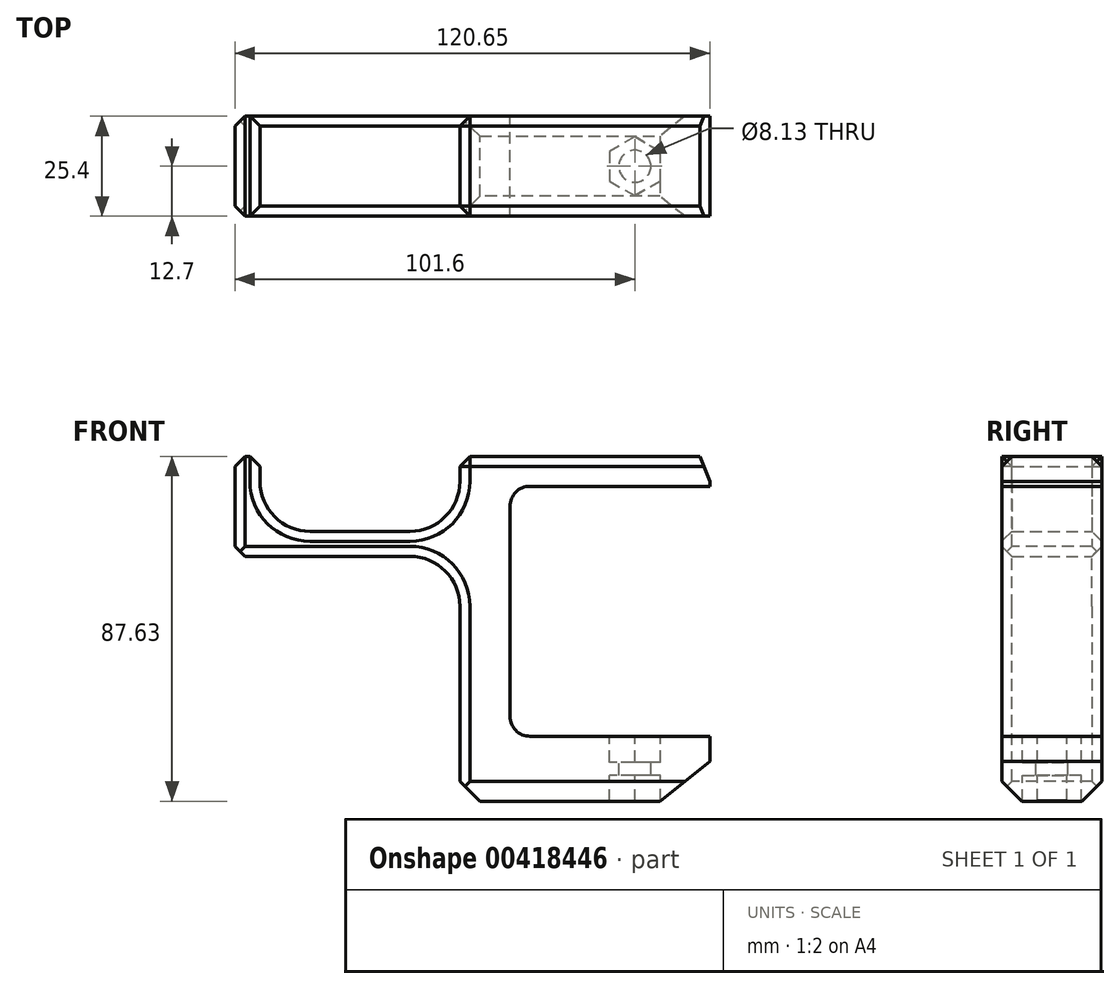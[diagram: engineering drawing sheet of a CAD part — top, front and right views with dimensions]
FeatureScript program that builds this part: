
annotation { "Feature Type Name" : "Feature", "Feature Type Description" : "" }
export const myFeature = defineFeature(function(context is Context, id is Id, definition is map)
    precondition{}
    {
        {
            var Q0;
            Q0=qCreatedBy(makeId("Front.planeOp"),FACE);
            var sketch = newSketch(context, id + "F0", { "sketchPlane" : qUnion([Q0])});
            skLineSegment(sketch, "E0.bottom", {"start": v(0, 44.53) * mm, "end": v(-12.7, 44.53) * mm});
            skLineSegment(sketch, "E0.top", {"start": v(0, -43.1) * mm, "end": v(-12.7, -43.1) * mm});
            skLineSegment(sketch, "E0.left", {"start": v(0, 44.53) * mm, "end": v(0, -43.1) * mm});
            skLineSegment(sketch, "E0.right", {"start": v(-12.7, 44.53) * mm, "end": v(-12.7, -43.1) * mm});
            skLineSegment(sketch, "E1.bottom", {"start": v(0, 44.53) * mm, "end": v(50.8, 44.53) * mm});
            skLineSegment(sketch, "E1.top", {"start": v(0, 36.9) * mm, "end": v(50.8, 36.9) * mm});
            skLineSegment(sketch, "E1.left", {"start": v(0, 44.53) * mm, "end": v(0, 36.9) * mm});
            skLineSegment(sketch, "E1.right", {"start": v(50.8, 44.53) * mm, "end": v(50.8, 36.9) * mm});
            skLineSegment(sketch, "E2.bottom", {"start": v(0, -43.1) * mm, "end": v(50.8, -43.1) * mm});
            skLineSegment(sketch, "E2.top", {"start": v(0, -26.6) * mm, "end": v(50.8, -26.6) * mm});
            skLineSegment(sketch, "E2.left", {"start": v(0, -43.1) * mm, "end": v(0, -26.6) * mm});
            skLineSegment(sketch, "E2.right", {"start": v(50.8, -43.1) * mm, "end": v(50.8, -26.6) * mm});
            skLineSegment(sketch, "E3.bottom", {"start": v(-12.7, 25.48) * mm, "end": v(-63.5, 25.48) * mm});
            skLineSegment(sketch, "E3.top", {"start": v(-12.7, 19.13) * mm, "end": v(-63.5, 19.13) * mm});
            skLineSegment(sketch, "E3.left", {"start": v(-12.7, 25.48) * mm, "end": v(-12.7, 19.13) * mm});
            skLineSegment(sketch, "E3.right", {"start": v(-63.5, 25.48) * mm, "end": v(-63.5, 19.13) * mm});
            skLineSegment(sketch, "E4.bottom", {"start": v(-63.5, 19.13) * mm, "end": v(-69.85, 19.13) * mm});
            skLineSegment(sketch, "E4.top", {"start": v(-63.5, 44.53) * mm, "end": v(-69.85, 44.53) * mm});
            skLineSegment(sketch, "E4.left", {"start": v(-63.5, 19.13) * mm, "end": v(-63.5, 44.53) * mm});
            skLineSegment(sketch, "E4.right", {"start": v(-69.85, 19.13) * mm, "end": v(-69.85, 44.53) * mm});
            skSolve(sketch);
        }
        {
            var Q0;
            {var subQ3=sQuery(id+"F0.wireOp",EDGE,"E4.bottom");Q0=makeQuery(id+"F0.imprint","IMPRINT",FACE,{"disambiguationData":[TD([[makeQuery(id+"F0.imprint","IMPRINT",EDGE,{"derivedFrom":subQ3}),-1.0]])]});}
            var Q1;
            {var subQ0=sQuery(id+"F0.wireOp",EDGE,"E3.bottom");Q1=makeQuery(id+"F0.imprint","IMPRINT",FACE,{"disambiguationData":[TD([[makeQuery(id+"F0.imprint","IMPRINT",EDGE,{"derivedFrom":subQ0}),1.0]])]});}
            var Q2;
            {var subQ1=sQuery(id+"F0.wireOp",EDGE,"E0.bottom");Q2=makeQuery(id+"F0.imprint","IMPRINT",FACE,{"disambiguationData":[TD([[makeQuery(id+"F0.imprint","IMPRINT",EDGE,{"derivedFrom":subQ1}),1.0]])]});}
            var Q3;
            Q3=makeQuery(id+"F0.imprint","IMPRINT",FACE,{"disambiguationData":[TD([[makeQuery(id+"F0.imprint","IMPRINT",EDGE,{"derivedFrom":sQuery(id+"F0.wireOp",EDGE,"E1.bottom")}),-1.0]])]});
            var Q4;
            Q4=makeQuery(id+"F0.imprint","IMPRINT",FACE,{"disambiguationData":[TD([[makeQuery(id+"F0.imprint","IMPRINT",EDGE,{"derivedFrom":sQuery(id+"F0.wireOp",EDGE,"E2.bottom")}),1.0]])]});
            extrude(context, id + "F1", {"entities" : qUnion([Q0, Q1, Q2, Q3, Q4]), "depth" : 25.4 * mm});
        }
        {
            var Q0;
            Q0=makeQuery(id+"F1.opExtrude","SWEPT_EDGE",EDGE,{"disambiguationData":[OSD([sQuery(id+"F0.wireOp",EDGE,"E0.right"),sQuery(id+"F0.wireOp",EDGE,"E3.bottom"),sQuery(id+"F0.wireOp",EDGE,"E3.left")])]});
            var Q1;
            Q1=makeQuery(id+"F1.opExtrude","SWEPT_EDGE",EDGE,{"disambiguationData":[OSD([sQuery(id+"F0.wireOp",EDGE,"E3.bottom"),sQuery(id+"F0.wireOp",EDGE,"E4.left")])]});
            fillet(context, id + "F2", {"entities" : qUnion([Q0, Q1]), "radius" : 12.7 * mm, "tangentPropagation" : true, "allowEdgeOverflow" : false});
        }
        {
            var Q0;
            Q0=makeQuery(id+"F1.opExtrude","SWEPT_EDGE",EDGE,{"disambiguationData":[OSD([sQuery(id+"F0.wireOp",EDGE,"E4.top"),sQuery(id+"F0.wireOp",EDGE,"E4.left")])]});
            var Q1;
            Q1=makeQuery(id+"F1.opExtrude","CAP_EDGE",EDGE,{"disambiguationData":[OSD([sQuery(id+"F0.wireOp",EDGE,"E4.right")])],"isStart":true});
            var Q2;
            Q2=makeQuery(id+"F1.opExtrude","SWEPT_EDGE",EDGE,{"disambiguationData":[OSD([sQuery(id+"F0.wireOp",EDGE,"E4.top"),sQuery(id+"F0.wireOp",EDGE,"E4.right")])]});
            var Q3;
            Q3=makeQuery(id+"F1.opExtrude","CAP_EDGE",EDGE,{"disambiguationData":[OSD([sQuery(id+"F0.wireOp",EDGE,"E4.right")])],"isStart":false});
            var Q4;
            {var subQ0=sQuery(id+"F0.wireOp",EDGE,"E4.left");var subQ1=sQuery(id+"F0.wireOp",EDGE,"E3.bottom");Q4=makeQuery(id+"F2.opFillet","BLEND_EDGE",EDGE,{"blendedFrom":[makeQuery(id+"F1.opExtrude","SWEPT_EDGE",EDGE,{"disambiguationData":[OSD([subQ1,subQ0])]}),makeQuery(id+"F1.opExtrude","CAP_FACE",FACE,{"disambiguationData":[OSD([sQuery(id+"F0.wireOp",EDGE,"E0.bottom"),sQuery(id+"F0.wireOp",EDGE,"E0.top"),sQuery(id+"F0.wireOp",EDGE,"E0.left"),sQuery(id+"F0.wireOp",EDGE,"E0.right"),sQuery(id+"F0.wireOp",EDGE,"E1.bottom"),sQuery(id+"F0.wireOp",EDGE,"E1.top"),sQuery(id+"F0.wireOp",EDGE,"E1.right"),sQuery(id+"F0.wireOp",EDGE,"E2.bottom"),sQuery(id+"F0.wireOp",EDGE,"E2.top"),sQuery(id+"F0.wireOp",EDGE,"E2.right"),subQ1,sQuery(id+"F0.wireOp",EDGE,"E3.top"),sQuery(id+"F0.wireOp",EDGE,"E4.bottom"),sQuery(id+"F0.wireOp",EDGE,"E4.top"),subQ0,sQuery(id+"F0.wireOp",EDGE,"E4.right")])],"isStart":false})],"blendedInto":[makeQuery(id+"F1.opExtrude","CAP_FACE",FACE,{"disambiguationData":[OSD([sQuery(id+"F0.wireOp",EDGE,"E0.bottom"),sQuery(id+"F0.wireOp",EDGE,"E0.top"),sQuery(id+"F0.wireOp",EDGE,"E0.left"),sQuery(id+"F0.wireOp",EDGE,"E0.right"),sQuery(id+"F0.wireOp",EDGE,"E1.bottom"),sQuery(id+"F0.wireOp",EDGE,"E1.top"),sQuery(id+"F0.wireOp",EDGE,"E1.right"),sQuery(id+"F0.wireOp",EDGE,"E2.bottom"),sQuery(id+"F0.wireOp",EDGE,"E2.top"),sQuery(id+"F0.wireOp",EDGE,"E2.right"),subQ1,sQuery(id+"F0.wireOp",EDGE,"E3.top"),sQuery(id+"F0.wireOp",EDGE,"E4.bottom"),sQuery(id+"F0.wireOp",EDGE,"E4.top"),subQ0,sQuery(id+"F0.wireOp",EDGE,"E4.right")])],"isStart":false})]});}
            var Q5;
            Q5=makeQuery(id+"F1.opExtrude","CAP_EDGE",EDGE,{"disambiguationData":[OSD([sQuery(id+"F0.wireOp",EDGE,"E3.bottom")])],"isStart":true});
            var Q6;
            Q6=makeQuery(id+"F1.opExtrude","SWEPT_EDGE",EDGE,{"disambiguationData":[OSD([sQuery(id+"F0.wireOp",EDGE,"E0.bottom"),sQuery(id+"F0.wireOp",EDGE,"E0.right")])]});
            var Q7;
            Q7=makeQuery(id+"F1.opExtrude","CAP_EDGE",EDGE,{"disambiguationData":[OSD([sQuery(id+"F0.wireOp",EDGE,"E0.bottom"),sQuery(id+"F0.wireOp",EDGE,"E1.bottom")])],"isStart":false});
            var Q8;
            Q8=makeQuery(id+"F1.opExtrude","CAP_EDGE",EDGE,{"disambiguationData":[OSD([sQuery(id+"F0.wireOp",EDGE,"E0.bottom"),sQuery(id+"F0.wireOp",EDGE,"E1.bottom")])],"isStart":true});
            var Q9;
            Q9=makeQuery(id+"F1.opExtrude","SWEPT_FACE",FACE,{"disambiguationData":[OSD([sQuery(id+"F0.wireOp",EDGE,"E4.right")])]});
            chamfer(context, id + "F3", {"entities" : qUnion([Q0, Q1, Q2, Q3, Q4, Q5, Q6, Q7, Q8, Q9]), "width" : 2.54 * mm, "tangentPropagation" : true});
        }
        {
            var Q0;
            Q0=makeQuery(id+"F1.opExtrude","SWEPT_EDGE",EDGE,{"disambiguationData":[OSD([sQuery(id+"F0.wireOp",EDGE,"E0.right"),sQuery(id+"F0.wireOp",EDGE,"E3.top"),sQuery(id+"F0.wireOp",EDGE,"E3.left")])]});
            fillet(context, id + "F4", {"entities" : qUnion([Q0]), "radius" : 12.7 * mm, "tangentPropagation" : true, "allowEdgeOverflow" : false});
        }
        {
            var Q0;
            {var subQ0=sQuery(id+"F0.wireOp",EDGE,"E0.right");Q0=makeQuery(id+"F1.opExtrude","CAP_EDGE",EDGE,{"disambiguationData":[OSD([subQ0]),TDD([makeQuery(id+"F0.imprint","IMPRINT",EDGE,{"disambiguationData":[TD([[makeQuery(id+"F0.imprint","INTERSECT",VERTEX,{"derivedFrom":[sQuery(id+"F0.wireOp",EDGE,"E0.top"),subQ0]}),1.0]])],"derivedFrom":subQ0})])],"isStart":false});}
            var Q1;
            {var subQ0=sQuery(id+"F0.wireOp",EDGE,"E0.right");Q1=makeQuery(id+"F1.opExtrude","CAP_EDGE",EDGE,{"disambiguationData":[OSD([subQ0]),TDD([makeQuery(id+"F0.imprint","IMPRINT",EDGE,{"disambiguationData":[TD([[makeQuery(id+"F0.imprint","INTERSECT",VERTEX,{"derivedFrom":[sQuery(id+"F0.wireOp",EDGE,"E0.top"),subQ0]}),1.0]])],"derivedFrom":subQ0})])],"isStart":true});}
            chamfer(context, id + "F5", {"entities" : qUnion([Q0, Q1]), "width" : 2.54 * mm, "tangentPropagation" : true});
        }
        {
            var Q0;
            Q0=makeQuery(id+"F1.opExtrude","SWEPT_EDGE",EDGE,{"disambiguationData":[OSD([sQuery(id+"F0.wireOp",EDGE,"E0.left"),sQuery(id+"F0.wireOp",EDGE,"E1.top"),sQuery(id+"F0.wireOp",EDGE,"E1.left")])]});
            var Q1;
            Q1=makeQuery(id+"F1.opExtrude","SWEPT_EDGE",EDGE,{"disambiguationData":[OSD([sQuery(id+"F0.wireOp",EDGE,"E0.left"),sQuery(id+"F0.wireOp",EDGE,"E2.top"),sQuery(id+"F0.wireOp",EDGE,"E2.left")])]});
            fillet(context, id + "F6", {"entities" : qUnion([Q0, Q1]), "radius" : 5.08 * mm, "tangentPropagation" : true, "allowEdgeOverflow" : false});
        }
        {
            var Q0;
            Q0=makeQuery(id+"F1.opExtrude","SWEPT_FACE",FACE,{"disambiguationData":[OSD([sQuery(id+"F0.wireOp",EDGE,"E2.top")])]});
            var sketch = newSketch(context, id + "F7", { "sketchPlane" : qUnion([Q0])});
            skPoint(sketch, "E5", {"position": v(31.75, -12.7) * mm});
            skCircle(sketch, "E6", {"center": v(31.75, -12.7) * mm, "radius": 6.48 * mm});
            skCircle(sketch, "E7.cCircle", {"center": v(31.75, -12.7) * mm, "radius": 6.48 * mm, "construction": true});
            skLineSegment(sketch, "E7.0", {"start": v(31.75, -5.22) * mm, "end": v(38.23, -8.96) * mm});
            skLineSegment(sketch, "E7.1", {"start": v(38.23, -8.96) * mm, "end": v(38.23, -16.44) * mm});
            skLineSegment(sketch, "E7.2", {"start": v(38.23, -16.44) * mm, "end": v(31.75, -20.18) * mm});
            skLineSegment(sketch, "E7.3", {"start": v(31.75, -20.18) * mm, "end": v(25.27, -16.44) * mm});
            skLineSegment(sketch, "E7.4", {"start": v(25.27, -16.44) * mm, "end": v(25.27, -8.96) * mm});
            skLineSegment(sketch, "E7.5", {"start": v(25.27, -8.96) * mm, "end": v(31.75, -5.22) * mm});
            skPoint(sketch, "E7.0.midPoint", {"position": v(34.99, -7.1) * mm});
            skSolve(sketch);
        }
        {
            var Q0;
            {var subQ0=sQuery(id+"F0.wireOp",EDGE,"E0.top");var subQ1=sQuery(id+"F0.wireOp",EDGE,"E0.right");Q0=makeQuery(id+"F5.opChamfer","BLEND_EDGE",EDGE,{"blendedFrom":[makeQuery(id+"F1.opExtrude","CAP_EDGE",EDGE,{"disambiguationData":[OSD([subQ1]),TDD([makeQuery(id+"F0.imprint","IMPRINT",EDGE,{"disambiguationData":[TD([[makeQuery(id+"F0.imprint","INTERSECT",VERTEX,{"derivedFrom":[subQ0,subQ1]}),1.0]])],"derivedFrom":subQ1})])],"isStart":false}),makeQuery(id+"F1.opExtrude","SWEPT_FACE",FACE,{"disambiguationData":[OSD([subQ0,sQuery(id+"F0.wireOp",EDGE,"E2.bottom")])]})],"blendedInto":[makeQuery(id+"F1.opExtrude","SWEPT_FACE",FACE,{"disambiguationData":[OSD([subQ0,sQuery(id+"F0.wireOp",EDGE,"E2.bottom")])]})]});}
            var Q1;
            Q1=makeQuery(id+"F1.opExtrude","SWEPT_EDGE",EDGE,{"disambiguationData":[OSD([sQuery(id+"F0.wireOp",EDGE,"E0.top"),sQuery(id+"F0.wireOp",EDGE,"E0.right")])]});
            var Q2;
            {var subQ0=sQuery(id+"F0.wireOp",EDGE,"E0.top");var subQ1=sQuery(id+"F0.wireOp",EDGE,"E0.right");Q2=makeQuery(id+"F5.opChamfer","BLEND_EDGE",EDGE,{"blendedFrom":[makeQuery(id+"F1.opExtrude","CAP_EDGE",EDGE,{"disambiguationData":[OSD([subQ1]),TDD([makeQuery(id+"F0.imprint","IMPRINT",EDGE,{"disambiguationData":[TD([[makeQuery(id+"F0.imprint","INTERSECT",VERTEX,{"derivedFrom":[subQ0,subQ1]}),1.0]])],"derivedFrom":subQ1})])],"isStart":true}),makeQuery(id+"F1.opExtrude","SWEPT_FACE",FACE,{"disambiguationData":[OSD([subQ0,sQuery(id+"F0.wireOp",EDGE,"E2.bottom")])]})],"blendedInto":[makeQuery(id+"F1.opExtrude","SWEPT_FACE",FACE,{"disambiguationData":[OSD([subQ0,sQuery(id+"F0.wireOp",EDGE,"E2.bottom")])]})]});}
            var Q3;
            Q3=makeQuery(id+"F1.opExtrude","CAP_EDGE",EDGE,{"disambiguationData":[OSD([sQuery(id+"F0.wireOp",EDGE,"E0.top"),sQuery(id+"F0.wireOp",EDGE,"E2.bottom")])],"isStart":true});
            var Q4;
            Q4=makeQuery(id+"F1.opExtrude","CAP_EDGE",EDGE,{"disambiguationData":[OSD([sQuery(id+"F0.wireOp",EDGE,"E0.top"),sQuery(id+"F0.wireOp",EDGE,"E2.bottom")])],"isStart":false});
            chamfer(context, id + "F8", {"entities" : qUnion([Q0, Q1, Q2, Q3, Q4]), "width" : 5.08 * mm, "tangentPropagation" : true});
        }
        {
            var Q0;
            Q0=makeQuery(id+"F1.opExtrude","SWEPT_EDGE",EDGE,{"disambiguationData":[OSD([sQuery(id+"F0.wireOp",EDGE,"E2.bottom"),sQuery(id+"F0.wireOp",EDGE,"E2.right")])]});
            chamfer(context, id + "F9", {"entities" : qUnion([Q0]), "chamferType" : ChamferType.TWO_OFFSETS, "width1" : 10.16 * mm, "oppositeDirection" : false, "width2" : 12.7 * mm, "tangentPropagation" : true});
        }
        {
            var Q0;
            Q0=makeQuery(id+"F1.opExtrude","SWEPT_EDGE",EDGE,{"disambiguationData":[OSD([sQuery(id+"F0.wireOp",EDGE,"E1.bottom"),sQuery(id+"F0.wireOp",EDGE,"E1.right")])]});
            chamfer(context, id + "F10", {"entities" : qUnion([Q0]), "chamferType" : ChamferType.TWO_OFFSETS, "width1" : 2.54 * mm, "oppositeDirection" : false, "width2" : 6.35 * mm, "tangentPropagation" : true});
        }
        {
            var Q0;
            {var subQ0=sQuery(id+"F7.wireOp",EDGE,"E7.4");var subQ1=sQuery(id+"F7.wireOp",EDGE,"E6");var subQ2=makeQuery(id+"F7.imprint","INTERSECT",VERTEX,{"derivedFrom":[subQ1,subQ0]});Q0=makeQuery(id+"F7.imprint","IMPRINT",FACE,{"disambiguationData":[TD([[makeQuery(id+"F7.imprint","IMPRINT",EDGE,{"disambiguationData":[TD([[subQ2,-1.0]])],"derivedFrom":subQ1}),-1.0]])]});}
            var Q1;
            {var subQ0=sQuery(id+"F7.wireOp",EDGE,"E7.5");var subQ1=sQuery(id+"F7.wireOp",EDGE,"E6");var subQ2=makeQuery(id+"F7.imprint","INTERSECT",VERTEX,{"derivedFrom":[subQ1,subQ0]});Q1=makeQuery(id+"F7.imprint","IMPRINT",FACE,{"disambiguationData":[TD([[makeQuery(id+"F7.imprint","IMPRINT",EDGE,{"disambiguationData":[TD([[subQ2,-1.0]])],"derivedFrom":subQ1}),-1.0]])]});}
            var Q2;
            {var subQ0=sQuery(id+"F7.wireOp",EDGE,"E7.0");var subQ1=sQuery(id+"F7.wireOp",EDGE,"E6");var subQ2=makeQuery(id+"F7.imprint","INTERSECT",VERTEX,{"derivedFrom":[subQ1,subQ0]});Q2=makeQuery(id+"F7.imprint","IMPRINT",FACE,{"disambiguationData":[TD([[makeQuery(id+"F7.imprint","IMPRINT",EDGE,{"disambiguationData":[TD([[subQ2,-1.0]])],"derivedFrom":subQ1}),-1.0]])]});}
            var Q3;
            {var subQ0=sQuery(id+"F7.wireOp",EDGE,"E7.0");var subQ1=sQuery(id+"F7.wireOp",EDGE,"E6");var subQ2=makeQuery(id+"F7.imprint","INTERSECT",VERTEX,{"derivedFrom":[subQ1,subQ0]});Q3=makeQuery(id+"F7.imprint","IMPRINT",FACE,{"disambiguationData":[TD([[makeQuery(id+"F7.imprint","IMPRINT",EDGE,{"disambiguationData":[TD([[subQ2,1.0]])],"derivedFrom":subQ1}),-1.0]])]});}
            var Q4;
            {var subQ0=sQuery(id+"F7.wireOp",EDGE,"E7.1");var subQ1=sQuery(id+"F7.wireOp",EDGE,"E6");var subQ2=makeQuery(id+"F7.imprint","INTERSECT",VERTEX,{"derivedFrom":[subQ1,subQ0]});Q4=makeQuery(id+"F7.imprint","IMPRINT",FACE,{"disambiguationData":[TD([[makeQuery(id+"F7.imprint","IMPRINT",EDGE,{"disambiguationData":[TD([[subQ2,1.0]])],"derivedFrom":subQ1}),-1.0]])]});}
            var Q5;
            {var subQ0=sQuery(id+"F7.wireOp",EDGE,"E7.3");var subQ1=sQuery(id+"F7.wireOp",EDGE,"E6");var subQ2=makeQuery(id+"F7.imprint","INTERSECT",VERTEX,{"derivedFrom":[subQ1,subQ0]});Q5=makeQuery(id+"F7.imprint","IMPRINT",FACE,{"disambiguationData":[TD([[makeQuery(id+"F7.imprint","IMPRINT",EDGE,{"disambiguationData":[TD([[subQ2,-1.0]])],"derivedFrom":subQ1}),-1.0]])]});}
            var Q6;
            {var subQ0=sQuery(id+"F7.wireOp",EDGE,"E6");var subQ4=makeQuery(id+"F7.imprint","INTERSECT",VERTEX,{"derivedFrom":[subQ0,sQuery(id+"F7.wireOp",EDGE,"E7.0")]});Q6=makeQuery(id+"F7.imprint","IMPRINT",FACE,{"disambiguationData":[TD([[makeQuery(id+"F7.imprint","IMPRINT",EDGE,{"disambiguationData":[TD([[subQ4,1.0]])],"derivedFrom":subQ0}),1.0]])]});}
            extrude(context, id + "F11", {"entities" : qUnion([Q0, Q1, Q2, Q3, Q4, Q5, Q6]), "operationType" : NewBodyOperationType.REMOVE, "oppositeDirection" : true, "depth" : 6.6 * mm});
        }
        {
            var Q0;
            {var subQ0=sQuery(id+"F7.wireOp",EDGE,"E6");var subQ4=makeQuery(id+"F7.imprint","INTERSECT",VERTEX,{"derivedFrom":[subQ0,sQuery(id+"F7.wireOp",EDGE,"E7.0")]});Q0=makeQuery(id+"F7.imprint","IMPRINT",FACE,{"disambiguationData":[TD([[makeQuery(id+"F7.imprint","IMPRINT",EDGE,{"disambiguationData":[TD([[subQ4,1.0]])],"derivedFrom":subQ0}),1.0]])]});}
            var Q1;
            {var subQ0=sQuery(id+"F7.wireOp",EDGE,"E7.1");var subQ1=sQuery(id+"F7.wireOp",EDGE,"E6");var subQ2=makeQuery(id+"F7.imprint","INTERSECT",VERTEX,{"derivedFrom":[subQ1,subQ0]});Q1=makeQuery(id+"F7.imprint","IMPRINT",FACE,{"disambiguationData":[TD([[makeQuery(id+"F7.imprint","IMPRINT",EDGE,{"disambiguationData":[TD([[subQ2,1.0]])],"derivedFrom":subQ1}),-1.0]])]});}
            var Q2;
            {var subQ0=sQuery(id+"F7.wireOp",EDGE,"E7.0");var subQ1=sQuery(id+"F7.wireOp",EDGE,"E6");var subQ2=makeQuery(id+"F7.imprint","INTERSECT",VERTEX,{"derivedFrom":[subQ1,subQ0]});Q2=makeQuery(id+"F7.imprint","IMPRINT",FACE,{"disambiguationData":[TD([[makeQuery(id+"F7.imprint","IMPRINT",EDGE,{"disambiguationData":[TD([[subQ2,-1.0]])],"derivedFrom":subQ1}),-1.0]])]});}
            var Q3;
            {var subQ0=sQuery(id+"F7.wireOp",EDGE,"E7.0");var subQ1=sQuery(id+"F7.wireOp",EDGE,"E6");var subQ2=makeQuery(id+"F7.imprint","INTERSECT",VERTEX,{"derivedFrom":[subQ1,subQ0]});Q3=makeQuery(id+"F7.imprint","IMPRINT",FACE,{"disambiguationData":[TD([[makeQuery(id+"F7.imprint","IMPRINT",EDGE,{"disambiguationData":[TD([[subQ2,1.0]])],"derivedFrom":subQ1}),-1.0]])]});}
            var Q4;
            {var subQ0=sQuery(id+"F7.wireOp",EDGE,"E7.5");var subQ1=sQuery(id+"F7.wireOp",EDGE,"E6");var subQ2=makeQuery(id+"F7.imprint","INTERSECT",VERTEX,{"derivedFrom":[subQ1,subQ0]});Q4=makeQuery(id+"F7.imprint","IMPRINT",FACE,{"disambiguationData":[TD([[makeQuery(id+"F7.imprint","IMPRINT",EDGE,{"disambiguationData":[TD([[subQ2,-1.0]])],"derivedFrom":subQ1}),-1.0]])]});}
            var Q5;
            {var subQ0=sQuery(id+"F7.wireOp",EDGE,"E7.4");var subQ1=sQuery(id+"F7.wireOp",EDGE,"E6");var subQ2=makeQuery(id+"F7.imprint","INTERSECT",VERTEX,{"derivedFrom":[subQ1,subQ0]});Q5=makeQuery(id+"F7.imprint","IMPRINT",FACE,{"disambiguationData":[TD([[makeQuery(id+"F7.imprint","IMPRINT",EDGE,{"disambiguationData":[TD([[subQ2,-1.0]])],"derivedFrom":subQ1}),-1.0]])]});}
            var Q6;
            {var subQ0=sQuery(id+"F7.wireOp",EDGE,"E7.3");var subQ1=sQuery(id+"F7.wireOp",EDGE,"E6");var subQ2=makeQuery(id+"F7.imprint","INTERSECT",VERTEX,{"derivedFrom":[subQ1,subQ0]});Q6=makeQuery(id+"F7.imprint","IMPRINT",FACE,{"disambiguationData":[TD([[makeQuery(id+"F7.imprint","IMPRINT",EDGE,{"disambiguationData":[TD([[subQ2,-1.0]])],"derivedFrom":subQ1}),-1.0]])]});}
            extrude(context, id + "F12", {"entities" : qUnion([Q0, Q1, Q2, Q3, Q4, Q5, Q6]), "operationType" : NewBodyOperationType.REMOVE, "endBound" : BoundingType.THROUGH_ALL, "oppositeDirection" : true, "depth" : -9.9 * mm, "hasSecondDirection" : true, "secondDirectionOppositeDirection" : true, "secondDirectionDepth" : 9.9 * mm});
        }
        {
            var Q0;
            Q0=sQuery(id+"F7.wireOp",VERTEX,"E5");
            var Q1;
            Q1=makeQuery(id+"F1.opExtrude","SWEPT_BODY",BODY,{"disambiguationData":[OSD([sQuery(id+"F0.wireOp",EDGE,"E0.bottom"),sQuery(id+"F0.wireOp",EDGE,"E0.top"),sQuery(id+"F0.wireOp",EDGE,"E0.left"),sQuery(id+"F0.wireOp",EDGE,"E0.right"),sQuery(id+"F0.wireOp",EDGE,"E1.bottom"),sQuery(id+"F0.wireOp",EDGE,"E1.top"),sQuery(id+"F0.wireOp",EDGE,"E1.right"),sQuery(id+"F0.wireOp",EDGE,"E2.bottom"),sQuery(id+"F0.wireOp",EDGE,"E2.top"),sQuery(id+"F0.wireOp",EDGE,"E2.right"),sQuery(id+"F0.wireOp",EDGE,"E3.bottom"),sQuery(id+"F0.wireOp",EDGE,"E3.top"),sQuery(id+"F0.wireOp",EDGE,"E4.bottom"),sQuery(id+"F0.wireOp",EDGE,"E4.top"),sQuery(id+"F0.wireOp",EDGE,"E4.left"),sQuery(id+"F0.wireOp",EDGE,"E4.right")])]});
            hole(context, id + "F13", {"style" : HoleStyle.SIMPLE, "endStyle" : HoleEndStyle.THROUGH, "holeDiameter" : 8.13 * mm, "isTappedThrough" : true, "tappedDepth" : 12.7 * mm, "tapClearance" : 3, "startFromSketch" : true, "locations" : qUnion([Q0]), "scope" : qUnion([Q1])});
        }
    });
